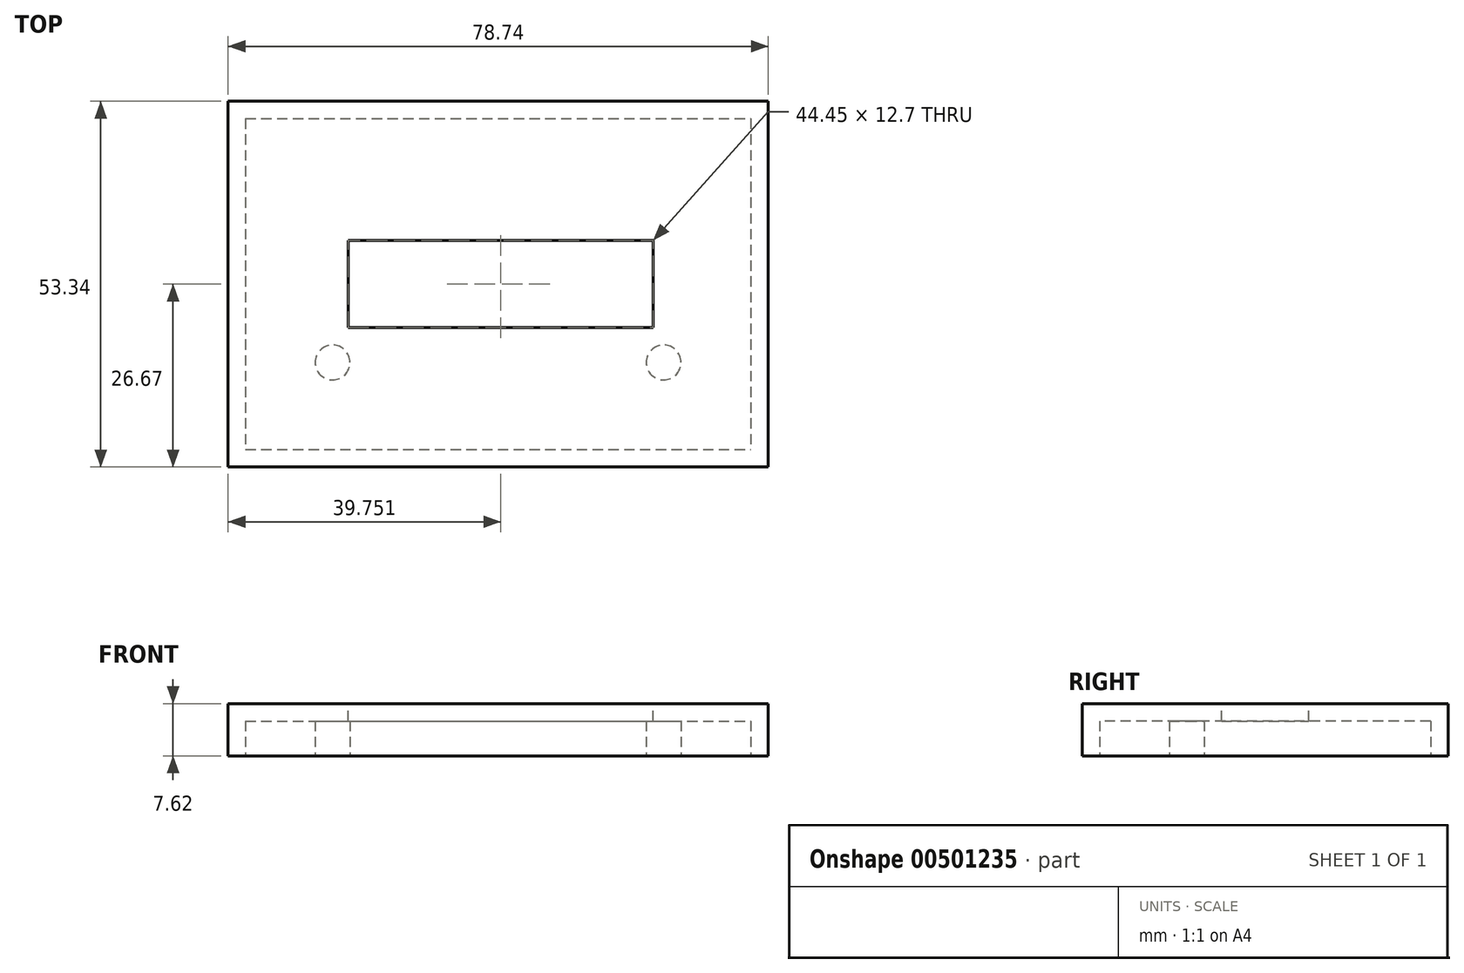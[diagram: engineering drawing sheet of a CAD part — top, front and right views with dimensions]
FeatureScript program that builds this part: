
annotation { "Feature Type Name" : "Feature", "Feature Type Description" : "" }
export const myFeature = defineFeature(function(context is Context, id is Id, definition is map)
    precondition{}
    {
        {
            var Q0;
            Q0=qCreatedBy(makeId("Top.planeOp"),FACE);
            var sketch = newSketch(context, id + "F0", { "sketchPlane" : qUnion([Q0])});
            skLineSegment(sketch, "E0.bottom", {"start": v(39.37, 26.67) * mm, "end": v(-39.37, 26.67) * mm});
            skLineSegment(sketch, "E0.top", {"start": v(39.37, -26.67) * mm, "end": v(-39.37, -26.67) * mm});
            skLineSegment(sketch, "E0.left", {"start": v(39.37, 26.67) * mm, "end": v(39.37, -26.67) * mm});
            skLineSegment(sketch, "E0.right", {"start": v(-39.37, 26.67) * mm, "end": v(-39.37, -26.67) * mm});
            skPoint(sketch, "E1", {"position": v(0, 26.67) * mm});
            skPoint(sketch, "E2", {"position": v(39.37, 0) * mm});
            skPoint(sketch, "E3", {"position": v(0, 0) * mm});
            skSolve(sketch);
        }
        {
            var Q0;
            Q0=makeQuery(id+"F0.imprint","IMPRINT",FACE,{"disambiguationData":[TD([[makeQuery(id+"F0.imprint","IMPRINT",EDGE,{"derivedFrom":sQuery(id+"F0.wireOp",EDGE,"E0.bottom")}),1.0]])]});
            extrude(context, id + "F1", {"entities" : qUnion([Q0]), "depth" : 7.62 * mm});
        }
        {
            var Q0;
            Q0=makeQuery(id+"F1.opExtrude","CAP_FACE",FACE,{"disambiguationData":[OSD([sQuery(id+"F0.wireOp",EDGE,"E0.bottom"),sQuery(id+"F0.wireOp",EDGE,"E0.top"),sQuery(id+"F0.wireOp",EDGE,"E0.left"),sQuery(id+"F0.wireOp",EDGE,"E0.right")])],"isStart":true});
            var sketch = newSketch(context, id + "F2", { "sketchPlane" : qUnion([Q0])});
            skSolve(sketch);
        }
        {
            var Q0;
            Q0=makeQuery(id+"F2.imprint","IMPRINT",FACE,{"disambiguationData":[TD([[makeQuery(id+"F2.imprint","IMPRINT",EDGE,{"derivedFrom":makeQuery(id+"F1.opExtrude","CAP_EDGE",EDGE,{"disambiguationData":[OSD([sQuery(id+"F0.wireOp",EDGE,"E0.bottom")])],"isStart":true})}),-1.0]])]});
            var sketch = newSketch(context, id + "F3", { "sketchPlane" : qUnion([Q0])});
            skLineSegment(sketch, "E4.bottom", {"start": v(-36.83, -24.13) * mm, "end": v(36.83, -24.13) * mm});
            skLineSegment(sketch, "E4.top", {"start": v(-36.83, 24.13) * mm, "end": v(36.83, 24.13) * mm});
            skLineSegment(sketch, "E4.left", {"start": v(-36.83, -24.13) * mm, "end": v(-36.83, 24.13) * mm});
            skLineSegment(sketch, "E4.right", {"start": v(36.83, -24.13) * mm, "end": v(36.83, 24.13) * mm});
            skSolve(sketch);
        }
        {
            var Q0;
            Q0 = qSketchRegion(id + "F3", true);
            extrude(context, id + "F4", {"entities" : qUnion([Q0]), "operationType" : NewBodyOperationType.REMOVE, "oppositeDirection" : true, "depth" : 5.08 * mm});
        }
        {
            var Q0;
            Q0=makeQuery(id+"F1.opExtrude","CAP_FACE",FACE,{"disambiguationData":[OSD([sQuery(id+"F0.wireOp",EDGE,"E0.bottom"),sQuery(id+"F0.wireOp",EDGE,"E0.top"),sQuery(id+"F0.wireOp",EDGE,"E0.left"),sQuery(id+"F0.wireOp",EDGE,"E0.right")])],"isStart":false});
            var sketch = newSketch(context, id + "F5", { "sketchPlane" : qUnion([Q0])});
            skLineSegment(sketch, "E5.bottom", {"start": v(22.6, 6.35) * mm, "end": v(-21.84, 6.35) * mm});
            skLineSegment(sketch, "E5.top", {"start": v(22.6, -6.35) * mm, "end": v(-21.84, -6.35) * mm});
            skLineSegment(sketch, "E5.left", {"start": v(22.6, 6.35) * mm, "end": v(22.6, -6.35) * mm});
            skLineSegment(sketch, "E5.right", {"start": v(-21.84, 6.35) * mm, "end": v(-21.84, -6.35) * mm});
            skSolve(sketch);
        }
        {
            var Q0;
            Q0 = qSketchRegion(id + "F5", true);
            extrude(context, id + "F6", {"entities" : qUnion([Q0]), "operationType" : NewBodyOperationType.REMOVE, "oppositeDirection" : true, "depth" : 25.4 * mm});
        }
        {
            var Q0;
            Q0=makeQuery(id+"F2.imprint","IMPRINT",FACE,{"disambiguationData":[TD([[makeQuery(id+"F2.imprint","IMPRINT",EDGE,{"derivedFrom":makeQuery(id+"F1.opExtrude","CAP_EDGE",EDGE,{"disambiguationData":[OSD([sQuery(id+"F0.wireOp",EDGE,"E0.bottom")])],"isStart":true})}),-1.0]])]});
            var sketch = newSketch(context, id + "F7", { "sketchPlane" : qUnion([Q0])});
            skPoint(sketch, "E6", {"position": v(24.13, 11.43) * mm});
            skPoint(sketch, "E7", {"position": v(-24.13, 11.43) * mm});
            skCircle(sketch, "E8", {"center": v(24.13, 11.43) * mm, "radius": 2.54 * mm});
            skCircle(sketch, "E9", {"center": v(-24.13, 11.43) * mm, "radius": 2.54 * mm});
            skSolve(sketch);
        }
        {
            var Q0;
            Q0 = qSketchRegion(id + "F7", true);
            extrude(context, id + "F8", {"entities" : qUnion([Q0]), "oppositeDirection" : true, "depth" : 5.08 * mm});
        }
    });
